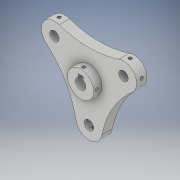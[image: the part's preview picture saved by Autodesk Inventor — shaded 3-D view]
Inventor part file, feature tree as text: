
AUTODESK INVENTOR PART (.ipt)
format: ipt  version: 2019 (Build 230136000, 136)  size: 258,560 bytes
history: native  units: mm
features: plane x10, sketch x9, hole x6, extrude x4, mirror x2, projected_geometry x2, other x1
ambient origin geometry x8: Origin, YZ Plane, XZ Plane, XY Plane, X Axis, Y Axis, Z Axis, Center Point
bodies: Body1 (feature_tree)
feature tree (34):
  other  "實體1"
  extrude  "擠出1"  Depth=109.5mm
  extrude  "擠出2"  Depth=43.5mm
  extrude  "擠出3"  Depth=76.5mm
  extrude  "擠出4"  Depth=25.0mm
  plane  "工作平面1"
  plane  "工作平面2"
  sketch  "草圖5"
  sketch  "草圖6"
  hole  "孔1"  [1 undecoded]
  hole  "孔2"  [1 undecoded]
  plane  "工作平面4"
  plane  "工作平面9"
  plane  "工作平面11"
  plane  "工作平面12"
  sketch  "草圖10"
  sketch  "草圖11"
  hole  "孔3"  [1 undecoded]
  hole  "孔4"  [1 undecoded]
  mirror  "鏡射1"
  hole  "孔5"  [1 undecoded]
  mirror  "鏡射2"
  plane  "工作平面14"
  plane  "工作平面15"
  hole  "孔7"  [1 undecoded]
  sketch  "草圖1"
  projected_geometry  "投影迴路1"
  sketch  "草圖3"
  sketch  "草圖4"
  projected_geometry  "投影迴路2"
  plane  "工作平面10"
  sketch  "草圖14"
  plane  "工作平面13"
  sketch  "草圖16"
note: 6 required parameter values undecoded (feature->parameter linkage not recoverable at this tier; creation-order binding heuristic only, values carry confidence <= 0.55)
